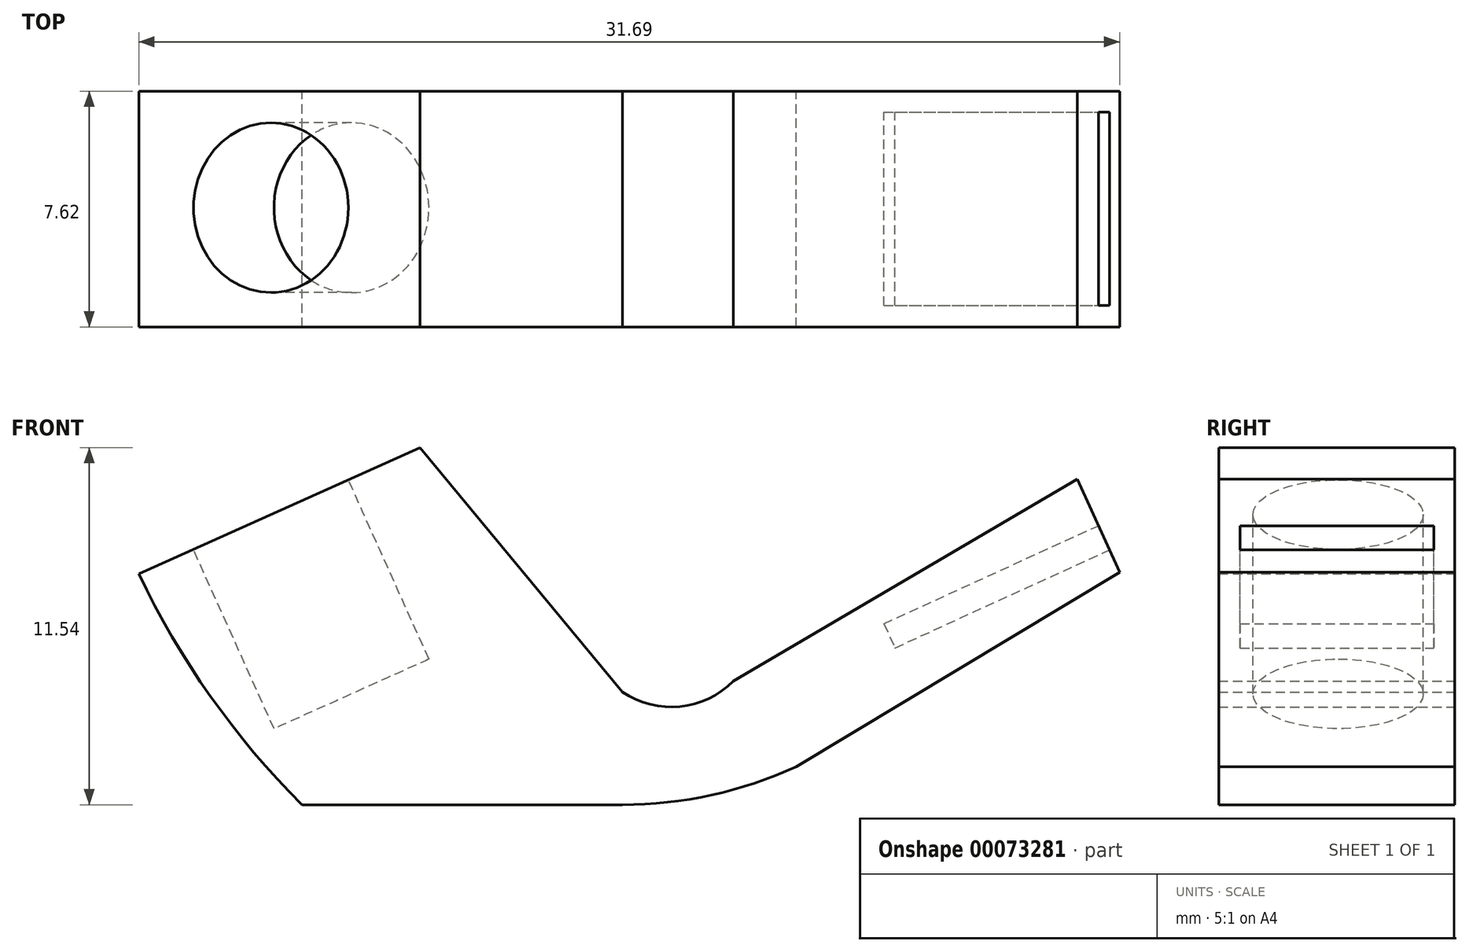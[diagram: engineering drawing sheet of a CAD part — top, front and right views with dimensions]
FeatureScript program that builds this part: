
annotation { "Feature Type Name" : "Feature", "Feature Type Description" : "" }
export const myFeature = defineFeature(function(context is Context, id is Id, definition is map)
    precondition{}
    {
        {
            var Q0;
            Q0=qCreatedBy(makeId("Front.planeOp"),FACE);
            var sketch = newSketch(context, id + "F0", { "sketchPlane" : qUnion([Q0])});
            skLineSegment(sketch, "E0", {"start": v(0, 0) * mm, "end": v(-10.36, 0) * mm});
            skArc(sketch, "E1", {"start": v(-15.63, 7.46) * mm, "mid": v(-13.31, 3.5) * mm, "end": v(-10.36, 0) * mm});
            skLineSegment(sketch, "E2", {"start": v(-15.63, 7.46) * mm, "end": v(-6.54, 11.54) * mm});
            skLineSegment(sketch, "E3", {"start": v(-6.54, 11.54) * mm, "end": v(0, 3.65) * mm});
            skLineSegment(sketch, "E4", {"start": v(16.06, 7.52) * mm, "end": v(14.69, 10.52) * mm});
            skArc(sketch, "E5", {"start": v(0, 3.65) * mm, "mid": v(1.85, 3.17) * mm, "end": v(3.58, 4) * mm});
            skLineSegment(sketch, "E6", {"start": v(14.69, 10.52) * mm, "end": v(3.58, 4) * mm});
            skArc(sketch, "E7", {"start": v(0, 0) * mm, "mid": v(2.87, 0.31) * mm, "end": v(5.61, 1.23) * mm});
            skLineSegment(sketch, "E8", {"start": v(16.06, 7.52) * mm, "end": v(5.61, 1.23) * mm});
            skLineSegment(sketch, "E9", {"start": v(0, 3.65) * mm, "end": v(0, 0) * mm});
            skSolve(sketch);
        }
        {
            var Q0;
            Q0=makeQuery(id+"F0.imprint","IMPRINT",FACE,{"disambiguationData":[TD([[makeQuery(id+"F0.imprint","IMPRINT",EDGE,{"derivedFrom":sQuery(id+"F0.wireOp",EDGE,"E0")}),-1.0]])]});
            extrude(context, id + "F1", {"entities" : qUnion([Q0]), "depth" : 7.62 * mm});
        }
        {
            var Q0;
            Q0=makeQuery(id+"F0.imprint","IMPRINT",FACE,{"disambiguationData":[TD([[makeQuery(id+"F0.imprint","IMPRINT",EDGE,{"derivedFrom":sQuery(id+"F0.wireOp",EDGE,"E4")}),1.0]])]});
            extrude(context, id + "F2", {"entities" : qUnion([Q0]), "operationType" : NewBodyOperationType.ADD, "depth" : 7.62 * mm});
        }
        {
            var Q0;
            Q0=makeQuery(id+"F1.opExtrude","SWEPT_FACE",FACE,{"disambiguationData":[OSD([sQuery(id+"F0.wireOp",EDGE,"E2")])]});
            var sketch = newSketch(context, id + "F3", { "sketchPlane" : qUnion([Q0])});
            skCircle(sketch, "E10", {"center": v(-6.52, -3.76) * mm, "radius": 2.74 * mm});
            skSolve(sketch);
        }
        {
            var Q0;
            Q0=makeQuery(id+"F3.imprint","IMPRINT",FACE,{"disambiguationData":[TD([[makeQuery(id+"F3.imprint","IMPRINT",EDGE,{"derivedFrom":sQuery(id+"F3.wireOp",EDGE,"E10")}),1.0]])]});
            extrude(context, id + "F4", {"entities" : qUnion([Q0]), "operationType" : NewBodyOperationType.REMOVE, "oppositeDirection" : true, "depth" : 6.35 * mm});
        }
        {
            var Q0;
            Q0=makeQuery(id+"F2.opExtrude","SWEPT_FACE",FACE,{"disambiguationData":[OSD([sQuery(id+"F0.wireOp",EDGE,"E4")])]});
            var sketch = newSketch(context, id + "F5", { "sketchPlane" : qUnion([Q0])});
            skPoint(sketch, "E11.firstSnap0", {"position": v(-7.62, 1.82) * mm});
            skLineSegment(sketch, "E11.bottom", {"start": v(-6.93, 1.82) * mm, "end": v(-0.67, 1.82) * mm});
            skLineSegment(sketch, "E11.top", {"start": v(-6.93, 0.96) * mm, "end": v(-0.67, 0.96) * mm});
            skLineSegment(sketch, "E11.left", {"start": v(-6.93, 1.82) * mm, "end": v(-6.93, 0.96) * mm});
            skLineSegment(sketch, "E11.right", {"start": v(-0.67, 1.82) * mm, "end": v(-0.67, 0.96) * mm});
            skSolve(sketch);
        }
        {
            var Q0;
            Q0=makeQuery(id+"F5.imprint","IMPRINT",FACE,{"disambiguationData":[TD([[makeQuery(id+"F5.imprint","IMPRINT",EDGE,{"derivedFrom":sQuery(id+"F5.wireOp",EDGE,"E11.bottom")}),-1.0]])]});
            extrude(context, id + "F6", {"entities" : qUnion([Q0]), "operationType" : NewBodyOperationType.REMOVE, "oppositeDirection" : true, "depth" : 7.62 * mm});
        }
    });
